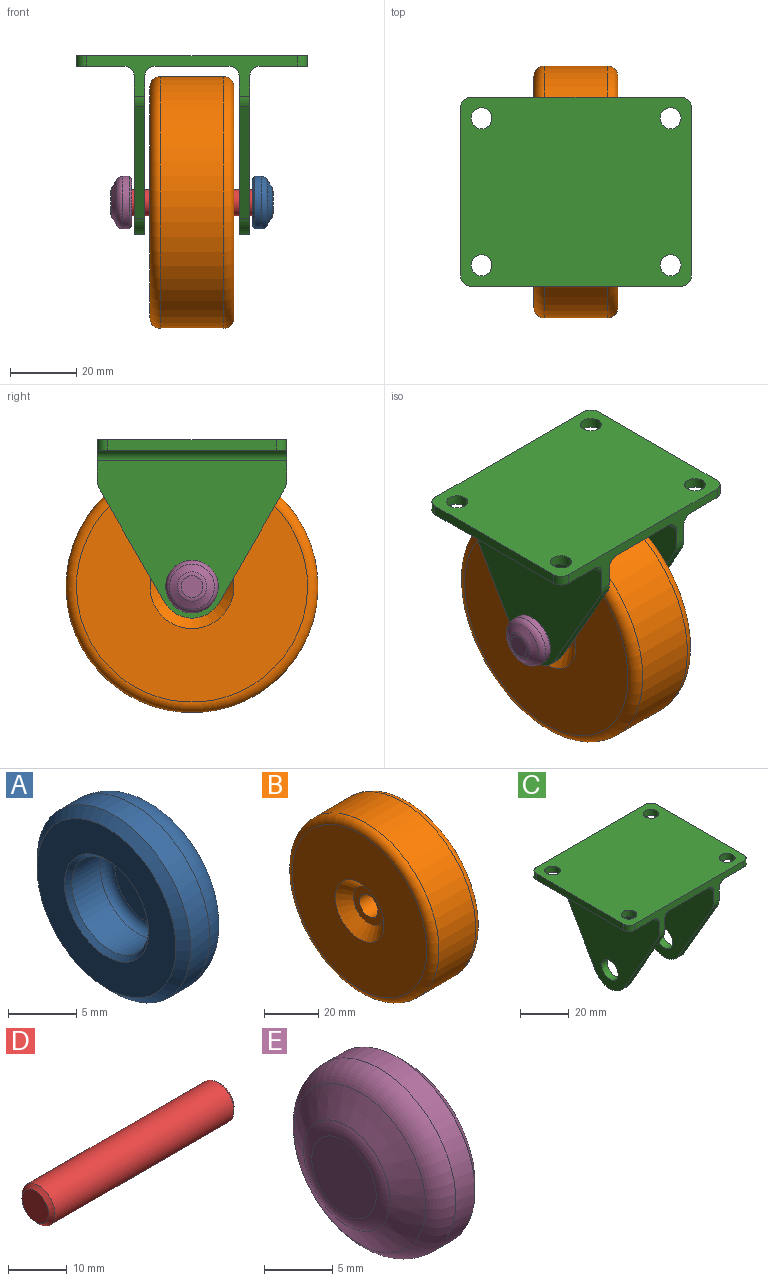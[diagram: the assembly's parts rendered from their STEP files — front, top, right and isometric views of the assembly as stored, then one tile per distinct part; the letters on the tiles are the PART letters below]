
ASSEMBLY  parts=5 mates=4
PART A: 11 faces, bbox 6.4x17.2x17.2 mm
  f0: plane 6.65x6.65mm, normal (1,0,0), area 34.7mm2, adj f6
  f1: cone r=3.94mm half-angle=60deg, axis (-1,0,0), area 95.1mm2, adj f6,f7
  f2: cylinder r=7.94mm len=15.88mm, axis (-1,0,0), area 97.7mm2, adj f7,f8
  f3: plane 14.35x14.35mm, normal (-1,0,0), area 102.5mm2, adj f8,f10
  f4: cylinder r=3.96mm len=7.92mm, axis (-1,0,0), area 72.7mm2, adj f9,f10
  f5: plane 6.4x6.4mm, normal (-1,0,0), area 32.2mm2, adj f9
  f6: torus R=3.32mm, axis (1,0,0), area 29.4mm2, adj f0,f1
  f7: torus R=5.65mm, axis (1,0,0), area 113.4mm2, adj f1,f2
  f8: cone r=7.18mm half-angle=45deg, axis (1,0,0), area 51.2mm2, adj f2,f3
  f9: torus R=3.2mm, axis (-1,0,0), area 27.7mm2, adj f4,f5
  f10: cone r=3.96mm half-angle=45deg, axis (-1,0,0), area 14.1mm2, adj f3,f4
PART B: 10 faces, bbox 25.4x82.5x82.5 mm
  f0: plane 69.85x69.85mm, normal (1,0,0), area 3325.3mm2, adj f1,f8
  f1: torus R=34.92mm, axis (-1,0,0), area 1157.7mm2, adj f0,f2
  f2: cylinder r=38.1mm len=76.2mm, axis (-1,0,0), area 4560.4mm2, adj f1,f3
  f3: torus R=34.92mm, axis (-1,0,0), area 1157.7mm2, adj f2,f4
  f4: plane 69.85x69.85mm, normal (-1,0,0), area 3325.3mm2, adj f3,f5
  f5: cone r=12.7mm half-angle=45deg, axis (-1,0,0), area 436.7mm2, adj f4,f6
  f6: plane 15.88x15.88mm, normal (-1,0,0), area 126.7mm2, adj f5,f9
  f7: plane 15.88x15.88mm, normal (1,0,0), area 126.7mm2, adj f8,f9
  f8: cone r=12.7mm half-angle=45deg, axis (1,0,0), area 436.7mm2, adj f0,f7
  f9: cylinder r=4.76mm len=15.88mm, axis (-1,0,0), area 475mm2, adj f6,f7
PART C: 36 faces, bbox 69.9x57.2x54 mm
  f0: plane 63.5x12.31mm, normal (0,-1,0), area 268.2mm2, adj f5,f6,f7,f11,f12,f13,f16,f17
  f1: plane 33.73x19.48mm, normal (0,-0.87,-0.5), area 123.7mm2, adj f2,f5,f6,f26
  f2: cylinder r=9.53mm len=16.5mm, axis (-1,0,0), area 63.3mm2, adj f1,f3,f5,f6
  f3: plane 33.73x19.48mm, normal (0,0.87,-0.5), area 123.7mm2, adj f2,f5,f6,f27
  f4: plane 63.5x12.31mm, normal (0,1,0), area 268.2mm2, adj f5,f6,f7,f11,f12,f13,f16,f17
  f5: plane 57.15x47.63mm, normal (1,0,0), area 1718mm2, adj f0,f1,f2,f3,f4,f19,f26,f27
  f6: plane 57.15x47.63mm, normal (-1,0,0), area 1718mm2, adj f0,f1,f2,f3,f4,f19,f26,f27
  f7: plane 57.15x14.28mm, normal (0,0,-1), area 748.1mm2, adj f0,f4,f14,f22,f23,f31,f32,f33
  f8: plane 33.73x19.48mm, normal (0,-0.87,-0.5), area 123.7mm2, adj f9,f11,f12,f24
  f9: cylinder r=9.53mm len=16.5mm, axis (1,0,0), area 63.3mm2, adj f8,f10,f11,f12
  f10: plane 33.73x19.48mm, normal (0,0.87,-0.5), area 123.7mm2, adj f9,f11,f12,f25
  f11: plane 57.15x47.63mm, normal (-1,0,0), area 1718mm2, adj f0,f4,f8,f9,f10,f18,f24,f25
  f12: plane 57.15x47.63mm, normal (1,0,0), area 1718mm2, adj f0,f4,f8,f9,f10,f18,f24,f25
  f13: plane 57.15x22.25mm, normal (0,0,-1), area 1271.6mm2, adj f0,f4,f29,f30
  f14: plane 50.8x3.18mm, normal (1,0,0), area 161.3mm2, adj f7,f16,f32,f33
  f15: plane 50.8x3.18mm, normal (-1,0,0), area 161.3mm2, adj f16,f17,f34,f35
  f16: plane 69.85x57.15mm, normal (0,0,1), area 3856.6mm2, adj f0,f4,f14,f15,f20,f21,f22,f23
  f17: plane 57.15x14.28mm, normal (0,0,-1), area 748.1mm2, adj f0,f4,f15,f20,f21,f28,f34,f35
  f18: cylinder r=4.76mm len=9.53mm, axis (1,0,0), area 95mm2, adj f11,f12
  f19: cylinder r=4.76mm len=9.53mm, axis (1,0,0), area 95mm2, adj f5,f6
  f20: cylinder r=3.17mm len=6.35mm, axis (0,0,1), area 63.3mm2, adj f16,f17
  f21: cylinder r=3.17mm len=6.35mm, axis (0,0,1), area 63.3mm2, adj f16,f17
  f22: cylinder r=3.17mm len=6.35mm, axis (0,0,1), area 63.3mm2, adj f7,f16
  f23: cylinder r=3.17mm len=6.35mm, axis (0,0,1), area 63.3mm2, adj f7,f16
  f24: cylinder r=6.35mm len=3.18mm, axis (-1,0,0), area 10.6mm2, adj f0,f8,f11,f12
  f25: cylinder r=6.35mm len=3.18mm, axis (-1,0,0), area 10.6mm2, adj f4,f10,f11,f12
  f26: cylinder r=6.35mm len=3.18mm, axis (1,0,0), area 10.6mm2, adj f0,f1,f5,f6
  f27: cylinder r=6.35mm len=3.18mm, axis (1,0,0), area 10.6mm2, adj f3,f4,f5,f6
  f28: cylinder r=3.17mm len=57.15mm, axis (0,1,0), area 285mm2, adj f0,f4,f11,f17
  f29: cylinder r=3.17mm len=57.15mm, axis (0,-1,0), area 285mm2, adj f0,f4,f12,f13
  f30: cylinder r=3.17mm len=57.15mm, axis (0,-1,0), area 285mm2, adj f0,f4,f6,f13
  f31: cylinder r=3.17mm len=57.15mm, axis (0,1,0), area 285mm2, adj f0,f4,f5,f7
  f32: cylinder r=3.17mm len=3.18mm, axis (0,0,1), area 15.8mm2, adj f0,f7,f14,f16
  f33: cylinder r=3.17mm len=3.18mm, axis (0,0,-1), area 15.8mm2, adj f4,f7,f14,f16
  f34: cylinder r=3.17mm len=3.18mm, axis (0,0,1), area 15.8mm2, adj f4,f15,f16,f17
  f35: cylinder r=3.17mm len=3.18mm, axis (0,0,-1), area 15.8mm2, adj f0,f15,f16,f17
PART D: 5 faces, bbox 44.5x7.9x7.9 mm
  f0: cylinder r=3.96mm len=42.93mm, axis (-1,0,0), area 1068.7mm2, adj f3,f4
  f1: plane 6.4x6.4mm, normal (1,0,0), area 32.2mm2, adj f4
  f2: plane 6.4x6.4mm, normal (-1,0,0), area 32.2mm2, adj f3
  f3: cone r=3.96mm half-angle=45deg, axis (1,0,0), area 24.2mm2, adj f0,f2
  f4: cone r=3.2mm half-angle=45deg, axis (-1,0,0), area 24.2mm2, adj f0,f1
PART E: 11 faces, bbox 6.4x17.2x17.2 mm
  f0: plane 6.65x6.65mm, normal (-1,0,0), area 34.7mm2, adj f6
  f1: cone r=3.94mm half-angle=60deg, axis (1,0,0), area 95.1mm2, adj f6,f7
  f2: cylinder r=7.94mm len=15.88mm, axis (1,0,0), area 97.7mm2, adj f7,f8
  f3: plane 14.35x14.35mm, normal (1,0,0), area 102.5mm2, adj f8,f10
  f4: cylinder r=3.96mm len=7.92mm, axis (1,0,0), area 72.7mm2, adj f9,f10
  f5: plane 6.4x6.4mm, normal (1,0,0), area 32.2mm2, adj f9
  f6: torus R=3.32mm, axis (-1,0,0), area 29.4mm2, adj f0,f1
  f7: torus R=5.65mm, axis (-1,0,0), area 113.4mm2, adj f1,f2
  f8: cone r=7.18mm half-angle=45deg, axis (-1,0,0), area 51.2mm2, adj f2,f3
  f9: torus R=3.2mm, axis (1,0,0), area 27.7mm2, adj f4,f5
  f10: cone r=4.34mm half-angle=45deg, axis (1,0,0), area 14.1mm2, adj f3,f4
PLACE A t=(38.2,-6.31,3.18)mm
PLACE B t=(38.58,-6.31,3.18)mm
PLACE C t=(38.59,-6.31,3.18)mm
PLACE D t=(38.58,-6.31,3.18)mm
PLACE E t=(38.96,-6.31,3.18)mm
MATE revolute B.f2 <-> D.f0  axis (-1,0,0) through (38.58,-6.31,3.18)mm
MATE fastened A.f1 <-> D.f0  axis (-1,0,0) through (60.8,-6.31,3.18)mm
MATE fastened E.f1 <-> D.f0  axis (1,0,0) through (16.35,-6.31,3.18)mm
MATE revolute C.f2 <-> B.f2  axis (1,0,0) through (22.7,-6.31,3.18)mm
